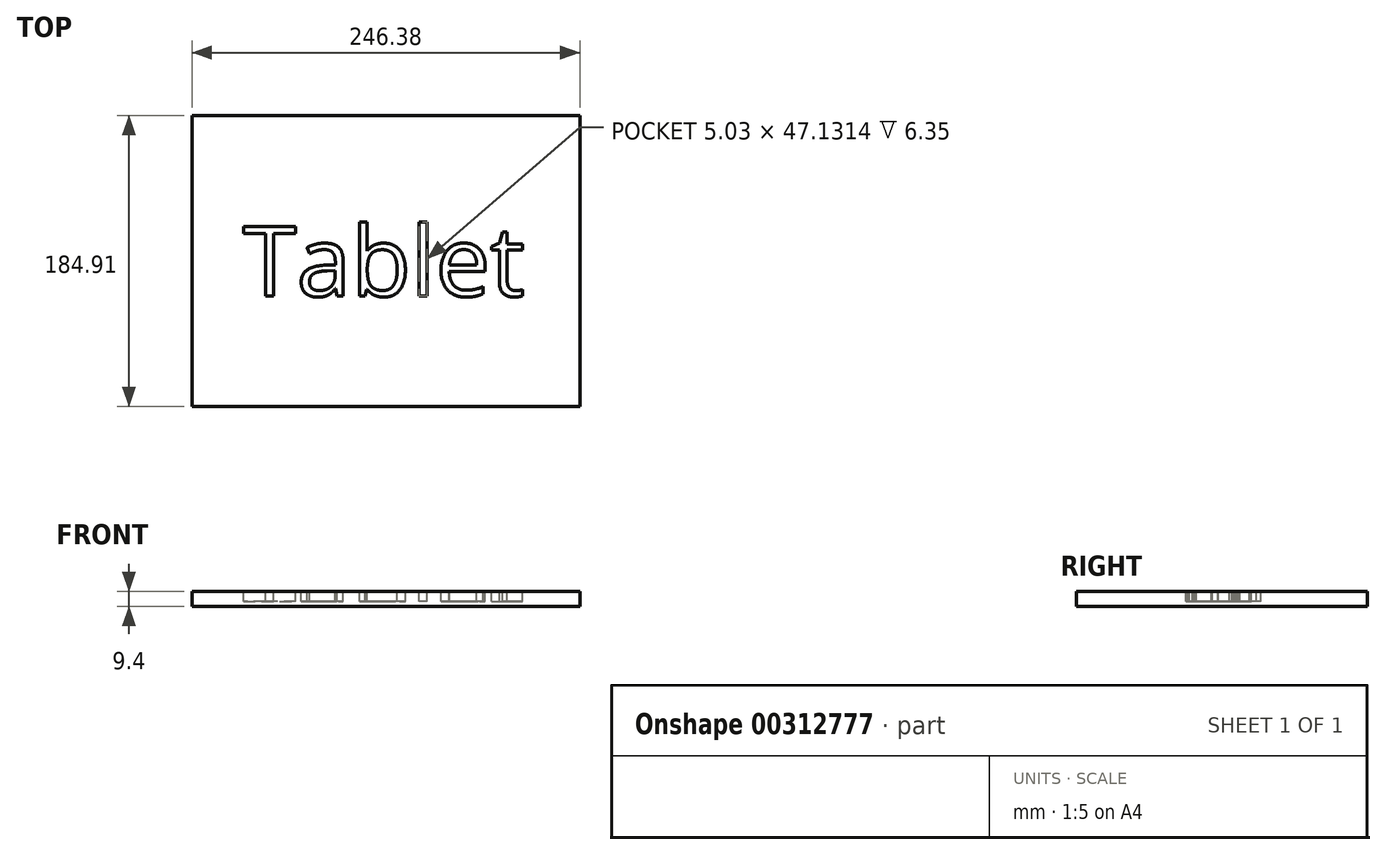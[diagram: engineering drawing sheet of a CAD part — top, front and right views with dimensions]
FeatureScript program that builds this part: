
annotation { "Feature Type Name" : "Feature", "Feature Type Description" : "" }
export const myFeature = defineFeature(function(context is Context, id is Id, definition is map)
    precondition{}
    {
        {
            var Q0;
            Q0=qCreatedBy(makeId("Top.planeOp"),FACE);
            var sketch = newSketch(context, id + "F0", { "sketchPlane" : qUnion([Q0])});
            skLineSegment(sketch, "E0.bottom", {"start": v(0, 0) * mm, "end": v(246.38, 0) * mm});
            skLineSegment(sketch, "E0.top", {"start": v(0, 184.91) * mm, "end": v(246.38, 184.91) * mm});
            skLineSegment(sketch, "E0.left", {"start": v(0, 0) * mm, "end": v(0, 184.91) * mm});
            skLineSegment(sketch, "E0.right", {"start": v(246.38, 0) * mm, "end": v(246.38, 184.91) * mm});
            skSolve(sketch);
        }
        {
            var Q0;
            Q0 = qSketchRegion(id + "F0", true);
            extrude(context, id + "F1", {"entities" : qUnion([Q0]), "depth" : 9.4 * mm});
        }
        {
            var Q0;
            Q0=makeQuery(id+"F1.opExtrude","CAP_FACE",FACE,{"disambiguationData":[OSD([sQuery(id+"F0.wireOp",EDGE,"E0.bottom"),sQuery(id+"F0.wireOp",EDGE,"E0.top"),sQuery(id+"F0.wireOp",EDGE,"E0.left"),sQuery(id+"F0.wireOp",EDGE,"E0.right")])],"isStart":false});
            var sketch = newSketch(context, id + "F2", { "sketchPlane" : qUnion([Q0])});
            skText(sketch, "E1", { "text": "Tablet", "fontName": "OpenSans-Regular.ttf"});
            skLineSegment(sketch, "E2", {"start": v(123.19, 114.79) * mm, "end": v(123.19, 184.91) * mm, "construction": true});
            skLineSegment(sketch, "E3", {"start": v(32.22, 92.46) * mm, "end": v(0, 92.46) * mm, "construction": true});
            const initialGuessF2  = {"E1": [0.03222, 0.07013, 1, 0, 0.04466]};
            skSetInitialGuess(sketch, initialGuessF2);
            skSolve(sketch);
        }
        {
            var Q0;
            Q0 = qSketchRegion(id + "F2", true);
            extrude(context, id + "F3", {"entities" : qUnion([Q0]), "operationType" : NewBodyOperationType.REMOVE, "oppositeDirection" : true, "depth" : 6.35 * mm});
        }
    });
